# Revit family: 346303xxS--Vitreous china wall-hung WC with horizontal outlet-Victoria-346303xxS
name_source: partatom
category: Plumbing Fixtures
units: mm (PartAtom-declared; Revit-internal decimal feet)

## family parameters
Always vertical = Yes
Cut with Voids When Loaded = No
Host = Wall
OmniClass Number = 23.45.05.21.11
OmniClass Title = Water Closets
Part Type = Normal
Room Calculation Point = No
Round Connector Dimension = Use Diameter
Shared = No

## types (2) — shared parameters
BIMobject category = WC
Description = Vitreous china wall-hung WC with horizontal outlet
Drain Diameter = 102 mm  [stored 0.334646 ft]
Edition number = 1
Flushing system = Washdown
Height = 395 mm
IFC Classification = Sanitary Terminal
Installation type = Wall-hung
Length = 355 mm
Manufacturer URL = www.roca.com
Manufacturer name = Roca
Model = 346303..S
NBS Reference Code = 35-65-90-97
NBS Reference Description = Wc Systems
Nominal height = 39500
Nominal width = 52500
Outlet Type = Horizontal
Product Guid = 9b014324-8f22-4f0a-94ab-1d9863f9d6b5
Product data url = http://bimobject.com
Product family = Victoria|Laura
Product group = TOILETS
QR code = https://www.roca.com
Shape = Round
URL = http://www.export.roca.com
Uniclass 1.4 Code = L7216
Uniclass 1.4 Description = Toilets
Uniclass 2.0 Code = SS-35-65-90-97
Uniclass 2.0 Description = Wc Systems
Water Inlet Diameter = 55 mm  [stored 0.180446 ft]
Width = 525 mm
zero-valued in all types: Weight Net (Kg)

## per-type parameters (varying)
| type | Imported Category Visibility 01 | Imported Category Visibility 02 | Primary Material | Product SKU |
| 34630300S White | Yes | No | White-Victoria-Roca | 34630300S |
| 34630317S Pergamon | No | Yes | Pergamon-Victoria-Roca | 34630317S |

note: [stored X ft] marks values corroborated as IEEE doubles in the binary element streams (Revit-internal decimal feet)

## geometry (parser evidence)
native form markers: Blend x4, Sweep x5
no freeform markers — native parametric forms only
